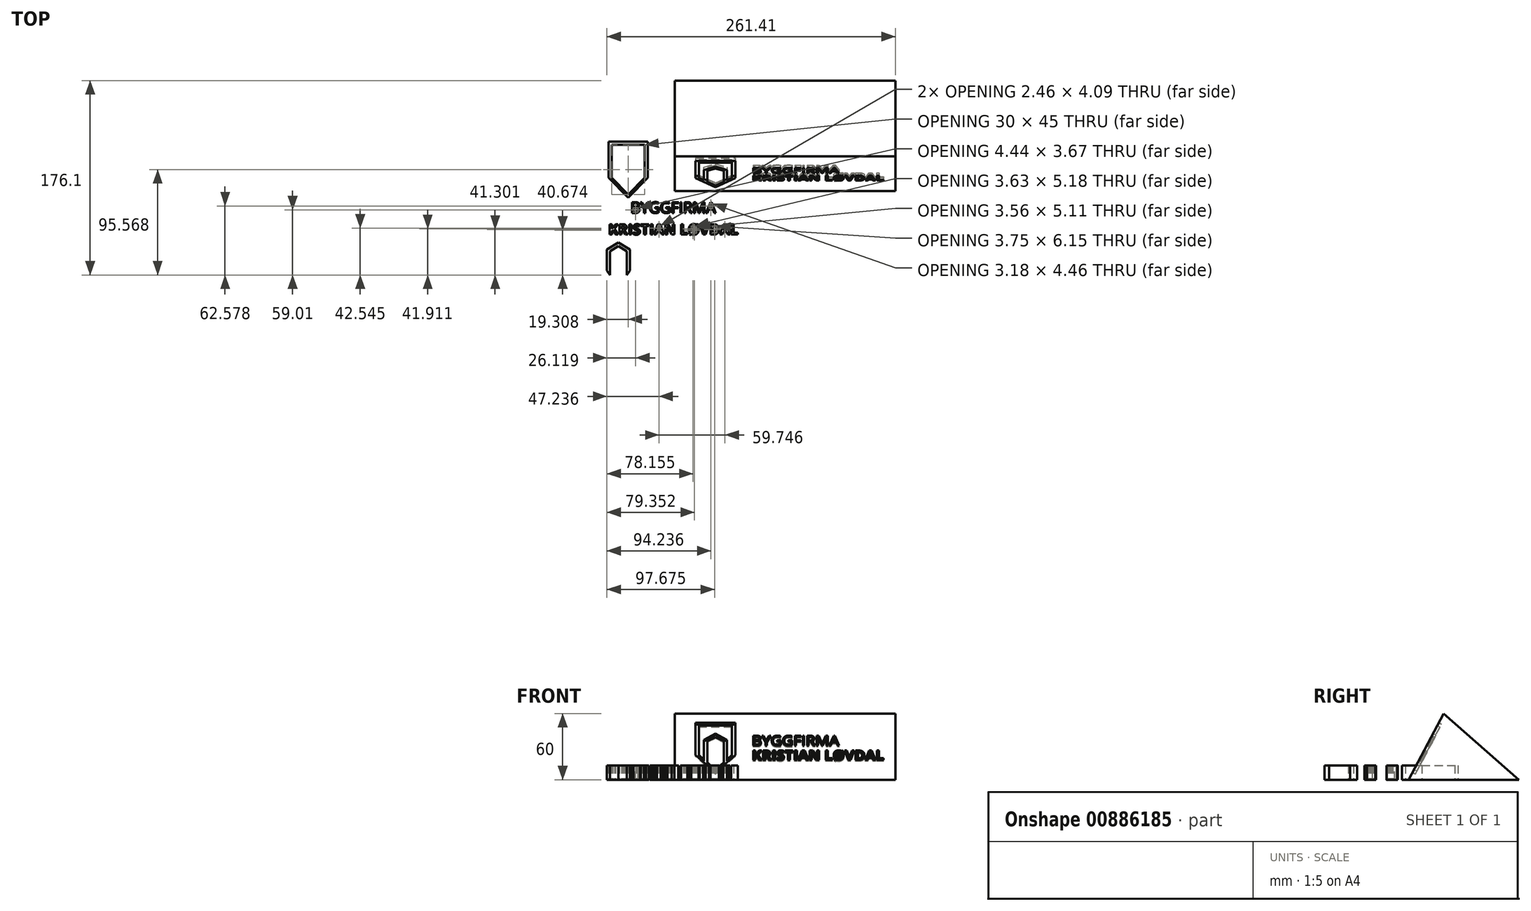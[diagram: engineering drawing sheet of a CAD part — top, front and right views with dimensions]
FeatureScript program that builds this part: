
annotation { "Feature Type Name" : "Feature", "Feature Type Description" : "" }
export const myFeature = defineFeature(function(context is Context, id is Id, definition is map)
    precondition{}
    {
        {
            var Q0;
            Q0=qCreatedBy(makeId("Top.planeOp"),FACE);
            var sketch = newSketch(context, id + "F0", { "sketchPlane" : qUnion([Q0])});
            skLineSegment(sketch, "E0.bottom", {"start": v(-100, 100) * mm, "end": v(100, 100) * mm});
            skLineSegment(sketch, "E0.top", {"start": v(-100, 0) * mm, "end": v(100, 0) * mm});
            skLineSegment(sketch, "E0.left", {"start": v(-100, 100) * mm, "end": v(-100, 0) * mm});
            skLineSegment(sketch, "E0.right", {"start": v(100, 100) * mm, "end": v(100, 0) * mm});
            skSolve(sketch);
        }
        {
            var Q0;
            Q0=qCreatedBy(makeId("Right.planeOp"),FACE);
            var sketch = newSketch(context, id + "F1", { "sketchPlane" : qUnion([Q0])});
            skLineSegment(sketch, "E1", {"start": v(100, 0) * mm, "end": v(31.57, 60) * mm});
            skLineSegment(sketch, "E2", {"start": v(31.57, 60) * mm, "end": v(0, 0) * mm});
            skLineSegment(sketch, "E3", {"start": v(100, 0) * mm, "end": v(0, 0) * mm});
            skSolve(sketch);
        }
        {
            var Q0;
            Q0=makeQuery(id+"F1.imprint","IMPRINT",FACE,{"disambiguationData":[TD([[makeQuery(id+"F1.imprint","IMPRINT",EDGE,{"derivedFrom":sQuery(id+"F1.wireOp",EDGE,"E1")}),1.0]])]});
            extrude(context, id + "F2", {"entities" : qUnion([Q0]), "depth" : 200 * mm, "offsetDistance" : 25 * mm});
        }
        {
            var Q0;
            Q0=makeQuery(id+"F2.opExtrude","SWEPT_FACE",FACE,{"disambiguationData":[OSD([sQuery(id+"F1.wireOp",EDGE,"E2")])]});
            var sketch = newSketch(context, id + "F3", { "sketchPlane" : qUnion([Q0])});
            skText(sketch, "E4", { "text": "BYGGFIRMA", "fontName": "OpenSans-Regular.ttf"});
            const initialGuessF3  = {"E4": [0.07, 0.035, 1, 0, 0.01015]};
            skSetInitialGuess(sketch, initialGuessF3);
            skSolve(sketch);
        }
        {
            var Q0;
            Q0=makeQuery(id+"F3.imprint","IMPRINT",FACE,{"disambiguationData":[TD([[makeQuery(id+"F3.imprint","IMPRINT",EDGE,{"derivedFrom":sQuery(id+"F3.wireOp",EDGE,"E4.sketch_text.stroke-0")}),1.0]])]});
            var sketch = newSketch(context, id + "F4", { "sketchPlane" : qUnion([Q0])});
            skText(sketch, "E5", { "text": "KRISTIAN LØVDAL", "fontName": "OpenSans-Bold.ttf"});
            const initialGuessF4  = {"E5": [0.07, 0.0203, 1, 0, 0.0097]};
            skSetInitialGuess(sketch, initialGuessF4);
            skSolve(sketch);
        }
        {
            var Q0;
            Q0 = qSketchRegion(id + "F4", true);
            extrude(context, id + "F5", {"entities" : qUnion([Q0]), "operationType" : NewBodyOperationType.REMOVE, "oppositeDirection" : true, "depth" : 3 * mm, "offsetDistance" : 25 * mm});
        }
        {
            var Q0;
            Q0 = qSketchRegion(id + "F3", true);
            extrude(context, id + "F6", {"entities" : qUnion([Q0]), "operationType" : NewBodyOperationType.REMOVE, "oppositeDirection" : true, "depth" : 3 * mm, "offsetDistance" : 25 * mm});
        }
        {
            var Q0;
            Q0=qCreatedBy(makeId("Top.planeOp"),FACE);
            var sketch = newSketch(context, id + "F7", { "sketchPlane" : qUnion([Q0])});
            skText(sketch, "E6", { "text": "BYGGFIRMA", "fontName": "OpenSans-Regular.ttf"});
            const initialGuessF7  = {"E6": [-0.04, -0.0199, 1, 0, 0.0099]};
            skSetInitialGuess(sketch, initialGuessF7);
            skSolve(sketch);
        }
        {
            var Q0;
            Q0=qCreatedBy(makeId("Top.planeOp"),FACE);
            var sketch = newSketch(context, id + "F8", { "sketchPlane" : qUnion([Q0])});
            skText(sketch, "E7", { "text": "KRISTIAN LØVDAL", "fontName": "OpenSans-Bold.ttf"});
            const initialGuessF8  = {"E7": [-0.06, -0.03953, 1, 0, 0.00953]};
            skSetInitialGuess(sketch, initialGuessF8);
            skSolve(sketch);
        }
        {
            var Q0;
            Q0 = qSketchRegion(id + "F7", true);
            extrude(context, id + "F9", {"entities" : qUnion([Q0]), "operationType" : NewBodyOperationType.ADD, "depth" : 13 * mm, "offsetDistance" : 25 * mm});
        }
        {
            var Q0;
            Q0 = qSketchRegion(id + "F8", true);
            extrude(context, id + "F10", {"entities" : qUnion([Q0]), "operationType" : NewBodyOperationType.ADD, "depth" : 13 * mm, "offsetDistance" : 25 * mm});
        }
        {
            var Q0;
            {var subQ76=sQuery(id+"F1.wireOp",EDGE,"E1");var subQ77=makeQuery(id+"F2.opExtrude","SWEPT_FACE",FACE,{"disambiguationData":[OSD([subQ76])]});var subQ82=sQuery(id+"F1.wireOp",EDGE,"E2");Q0=makeQuery(id+"F6.boolean.opBoolean","SPLIT",FACE,{"disambiguationData":[TD([subQ77])],"derivedFrom":makeQuery(id+"F5.boolean.opBoolean","SPLIT",FACE,{"disambiguationData":[TD([subQ77])],"derivedFrom":makeQuery(id+"F2.opExtrude","SWEPT_FACE",FACE,{"disambiguationData":[OSD([subQ82])]})})});}
            var sketch = newSketch(context, id + "F11", { "sketchPlane" : qUnion([Q0])});
            skLineSegment(sketch, "E8", {"start": v(52, 55.3) * mm, "end": v(22, 55.3) * mm});
            skLineSegment(sketch, "E9", {"start": v(22, 55.3) * mm, "end": v(22, 25.3) * mm});
            skLineSegment(sketch, "E10", {"start": v(22, 25.3) * mm, "end": v(37, 10.3) * mm});
            skLineSegment(sketch, "E11", {"start": v(37, 10.3) * mm, "end": v(52, 25.3) * mm});
            skLineSegment(sketch, "E12", {"start": v(52, 25.3) * mm, "end": v(52, 55.3) * mm});
            skSolve(sketch);
        }
        {
            var Q0;
            Q0=makeQuery(id+"F11.imprint","IMPRINT",FACE,{"disambiguationData":[TD([[makeQuery(id+"F11.imprint","IMPRINT",EDGE,{"derivedFrom":sQuery(id+"F11.wireOp",EDGE,"E8")}),1.0]])]});
            var sketch = newSketch(context, id + "F12", { "sketchPlane" : qUnion([Q0])});
            skLineSegment(sketch, "E13", {"start": v(19, 58.3) * mm, "end": v(55, 58.3) * mm});
            skLineSegment(sketch, "E14", {"start": v(55, 58.3) * mm, "end": v(55, 25.3) * mm});
            skLineSegment(sketch, "E15", {"start": v(55, 25.3) * mm, "end": v(37, 7.3) * mm});
            skLineSegment(sketch, "E16", {"start": v(37, 7.3) * mm, "end": v(19, 25.3) * mm});
            skLineSegment(sketch, "E17", {"start": v(19, 25.3) * mm, "end": v(19, 58.3) * mm});
            skSolve(sketch);
        }
        {
            var Q0;
            Q0=makeQuery(id+"F12.imprint","IMPRINT",FACE,{"disambiguationData":[TD([[makeQuery(id+"F12.imprint","IMPRINT",EDGE,{"derivedFrom":sQuery(id+"F12.wireOp",EDGE,"E13")}),-1.0]])]});
            extrude(context, id + "F13", {"entities" : qUnion([Q0]), "operationType" : NewBodyOperationType.REMOVE, "oppositeDirection" : true, "depth" : 3 * mm, "offsetDistance" : 25 * mm});
        }
        {
            var Q0;
            Q0=qCreatedBy(makeId("Top.planeOp"),FACE);
            var sketch = newSketch(context, id + "F14", { "sketchPlane" : qUnion([Q0])});
            skLineSegment(sketch, "E18", {"start": v(-57.1, 41.97) * mm, "end": v(-27.1, 41.97) * mm});
            skLineSegment(sketch, "E19", {"start": v(-27.1, 41.97) * mm, "end": v(-27.1, 11.97) * mm});
            skLineSegment(sketch, "E20", {"start": v(-27.1, 11.97) * mm, "end": v(-42.1, -3.03) * mm});
            skLineSegment(sketch, "E21", {"start": v(-42.1, -3.03) * mm, "end": v(-57.1, 11.97) * mm});
            skLineSegment(sketch, "E22", {"start": v(-57.1, 11.97) * mm, "end": v(-57.1, 41.97) * mm});
            skSolve(sketch);
        }
        {
            var Q0;
            Q0=qCreatedBy(makeId("Top.planeOp"),FACE);
            var sketch = newSketch(context, id + "F15", { "sketchPlane" : qUnion([Q0])});
            skLineSegment(sketch, "E23", {"start": v(-60, 44.87) * mm, "end": v(-24.2, 44.87) * mm});
            skLineSegment(sketch, "E24", {"start": v(-24.2, 44.87) * mm, "end": v(-24.2, 11.97) * mm});
            skLineSegment(sketch, "E25", {"start": v(-24.2, 11.97) * mm, "end": v(-42.1, -5.93) * mm});
            skLineSegment(sketch, "E26", {"start": v(-42.1, -5.93) * mm, "end": v(-60, 11.97) * mm});
            skLineSegment(sketch, "E27", {"start": v(-60, 11.97) * mm, "end": v(-60, 44.87) * mm});
            skSolve(sketch);
        }
        {
            var Q0;
            Q0 = qSketchRegion(id + "F15", true);
            extrude(context, id + "F16", {"entities" : qUnion([Q0]), "operationType" : NewBodyOperationType.ADD, "depth" : 13 * mm, "offsetDistance" : 25 * mm});
        }
        {
            var Q0;
            Q0 = qSketchRegion(id + "F14", true);
            extrude(context, id + "F17", {"entities" : qUnion([Q0]), "operationType" : NewBodyOperationType.REMOVE, "depth" : 25 * mm, "offsetDistance" : 25 * mm});
        }
        {
            var Q0;
            Q0=makeQuery(id+"F11.imprint","IMPRINT",FACE,{"disambiguationData":[TD([[makeQuery(id+"F11.imprint","IMPRINT",EDGE,{"derivedFrom":sQuery(id+"F11.wireOp",EDGE,"E8")}),1.0]])]});
            var sketch = newSketch(context, id + "F18", { "sketchPlane" : qUnion([Q0])});
            skLineSegment(sketch, "E28", {"start": v(26.5, 20.8) * mm, "end": v(26.5, 40.8) * mm});
            skLineSegment(sketch, "E29", {"start": v(26.5, 40.8) * mm, "end": v(37, 47.3) * mm});
            skLineSegment(sketch, "E30", {"start": v(37, 47.3) * mm, "end": v(47.5, 40.8) * mm});
            skLineSegment(sketch, "E31", {"start": v(47.5, 40.8) * mm, "end": v(47.5, 20.8) * mm});
            skLineSegment(sketch, "E32", {"start": v(47.5, 20.8) * mm, "end": v(44.5, 17.8) * mm});
            skLineSegment(sketch, "E33", {"start": v(44.5, 17.8) * mm, "end": v(44.5, 39.56) * mm});
            skLineSegment(sketch, "E34", {"start": v(44.5, 39.56) * mm, "end": v(37, 43.8) * mm});
            skLineSegment(sketch, "E35", {"start": v(37, 43.8) * mm, "end": v(29.5, 39.56) * mm});
            skLineSegment(sketch, "E36", {"start": v(29.5, 39.56) * mm, "end": v(29.5, 17.8) * mm});
            skLineSegment(sketch, "E37", {"start": v(29.5, 17.8) * mm, "end": v(26.5, 20.8) * mm});
            skSolve(sketch);
        }
        {
            var Q0;
            {var subQ4=sQuery(id+"F18.wireOp",EDGE,"E29");Q0=makeQuery(id+"F18.imprint","IMPRINT",FACE,{"disambiguationData":[TD([[makeQuery(id+"F18.imprint","IMPRINT",EDGE,{"derivedFrom":subQ4}),-1.0]])]});}
            extrude(context, id + "F19", {"entities" : qUnion([Q0]), "operationType" : NewBodyOperationType.REMOVE, "oppositeDirection" : true, "depth" : 3 * mm, "offsetDistance" : 25 * mm});
        }
        {
            var Q0;
            Q0=qCreatedBy(makeId("Top.planeOp"),FACE);
            var sketch = newSketch(context, id + "F20", { "sketchPlane" : qUnion([Q0])});
            skLineSegment(sketch, "E38", {"start": v(-61.41, -71.95) * mm, "end": v(-61.41, -52.95) * mm});
            skLineSegment(sketch, "E39", {"start": v(-61.41, -52.95) * mm, "end": v(-51.01, -46.6) * mm});
            skLineSegment(sketch, "E40", {"start": v(-51.01, -46.6) * mm, "end": v(-40.61, -52.95) * mm});
            skLineSegment(sketch, "E41", {"start": v(-40.61, -52.95) * mm, "end": v(-40.61, -71.95) * mm});
            skLineSegment(sketch, "E42", {"start": v(-40.61, -71.95) * mm, "end": v(-43.41, -76.1) * mm});
            skLineSegment(sketch, "E43", {"start": v(-43.41, -76.1) * mm, "end": v(-43.41, -54.54) * mm});
            skLineSegment(sketch, "E44", {"start": v(-43.41, -54.54) * mm, "end": v(-51.01, -49.9) * mm});
            skLineSegment(sketch, "E45", {"start": v(-51.01, -49.9) * mm, "end": v(-58.61, -54.54) * mm});
            skLineSegment(sketch, "E46", {"start": v(-58.61, -54.54) * mm, "end": v(-58.61, -76.1) * mm});
            skLineSegment(sketch, "E47", {"start": v(-58.61, -76.1) * mm, "end": v(-61.41, -71.95) * mm});
            skSolve(sketch);
        }
        {
            var Q0;
            Q0 = qSketchRegion(id + "F20", true);
            extrude(context, id + "F21", {"entities" : qUnion([Q0]), "operationType" : NewBodyOperationType.ADD, "depth" : 13 * mm, "offsetDistance" : 25 * mm});
        }
    });
